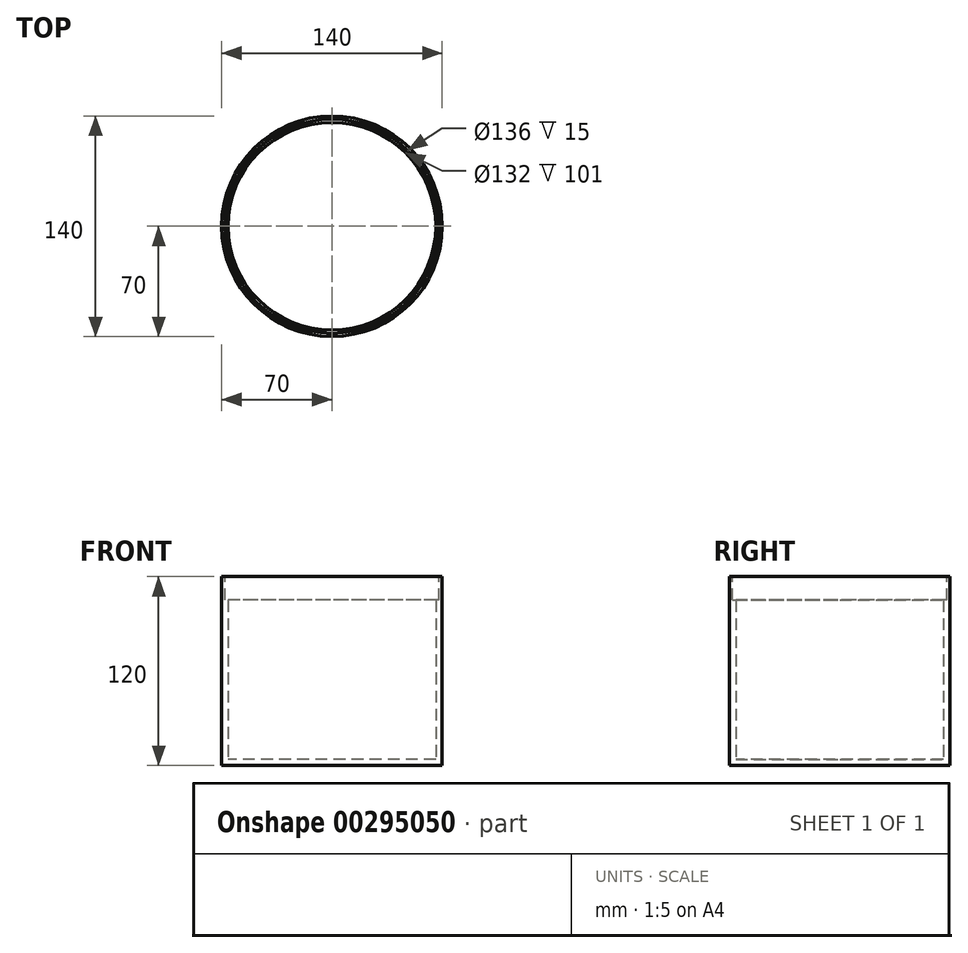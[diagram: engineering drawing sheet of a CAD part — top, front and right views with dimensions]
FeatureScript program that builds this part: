
annotation { "Feature Type Name" : "Feature", "Feature Type Description" : "" }
export const myFeature = defineFeature(function(context is Context, id is Id, definition is map)
    precondition{}
    {
        {
            var Q0;
            Q0=qCreatedBy(makeId("Top.planeOp"),FACE);
            var sketch = newSketch(context, id + "F0", { "sketchPlane" : qUnion([Q0])});
            skCircle(sketch, "E0", {"center": v(0, 0) * mm, "radius": 70 * mm});
            skSolve(sketch);
        }
        {
            var Q0;
            Q0 = qSketchRegion(id + "F0", true);
            extrude(context, id + "F1", {"entities" : qUnion([Q0]), "depth" : 120 * mm});
        }
        {
            var Q0;
            Q0=makeQuery(id+"F1.opExtrude","CAP_FACE",FACE,{"disambiguationData":[OSD([sQuery(id+"F0.wireOp",EDGE,"E0")])],"isStart":false});
            shell(context, id + "F2", {"entities" : qUnion([Q0]), "thickness" : 4 * mm});
        }
        {
            var Q0;
            Q0=makeQuery(id+"F1.opExtrude","CAP_FACE",FACE,{"disambiguationData":[OSD([sQuery(id+"F0.wireOp",EDGE,"E0")])],"isStart":false});
            var sketch = newSketch(context, id + "F3", { "sketchPlane" : qUnion([Q0])});
            skCircle(sketch, "E1", {"center": v(0, 0) * mm, "radius": 68 * mm});
            skSolve(sketch);
        }
        {
            var Q0;
            Q0 = qSketchRegion(id + "F3", true);
            extrude(context, id + "F4", {"entities" : qUnion([Q0]), "operationType" : NewBodyOperationType.REMOVE, "oppositeDirection" : true, "depth" : 15 * mm});
        }
    });
